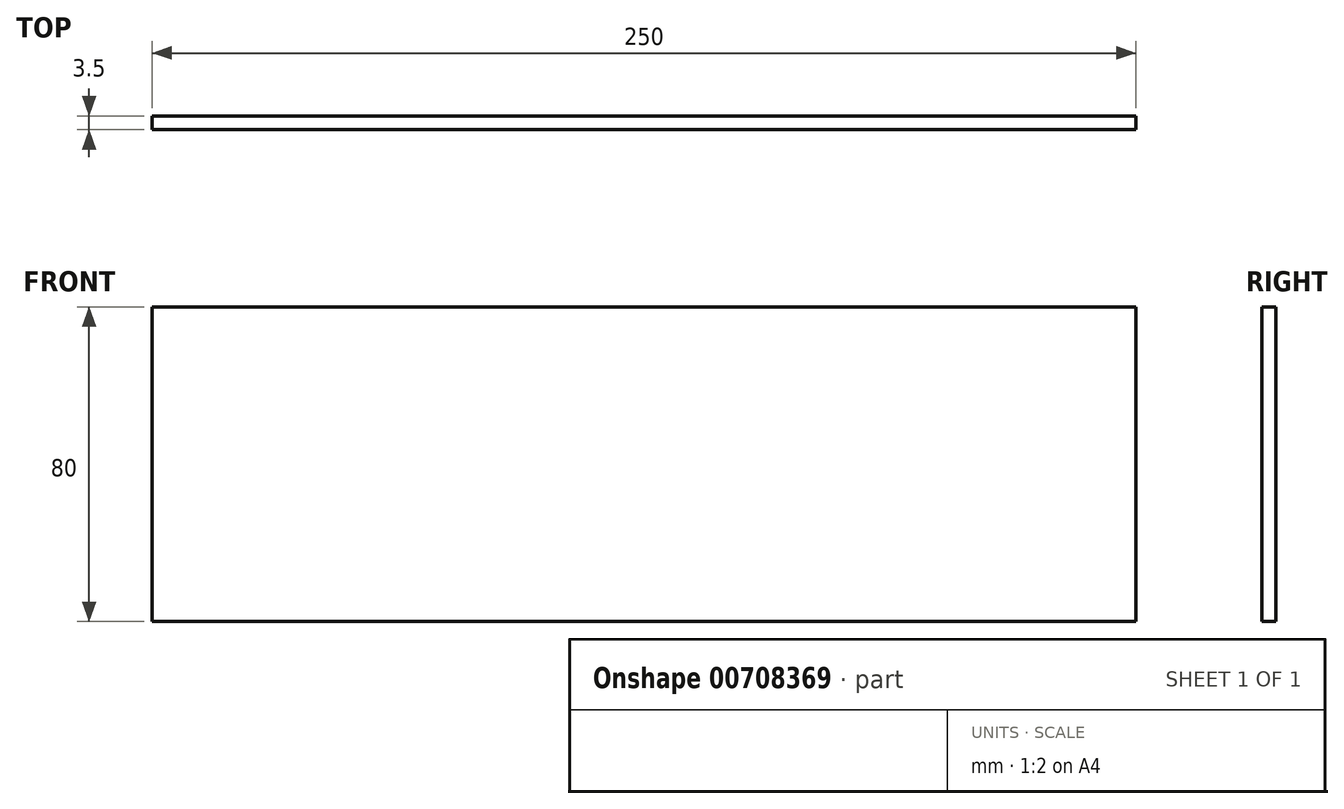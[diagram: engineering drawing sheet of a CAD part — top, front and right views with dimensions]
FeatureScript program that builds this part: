
annotation { "Feature Type Name" : "Feature", "Feature Type Description" : "" }
export const myFeature = defineFeature(function(context is Context, id is Id, definition is map)
    precondition{}
    {
        {
            var Q0;
            Q0=qCreatedBy(makeId("Right.planeOp"),FACE);
            var sketch = newSketch(context, id + "F0", { "sketchPlane" : qUnion([Q0])});
            skLineSegment(sketch, "E0", {"start": v(0, 0) * mm, "end": v(0, 80) * mm});
            skLineSegment(sketch, "E1", {"start": v(0, 80) * mm, "end": v(-3.5, 80) * mm});
            skLineSegment(sketch, "E2", {"start": v(-3.5, 80) * mm, "end": v(-3.5, 0) * mm});
            skLineSegment(sketch, "E3", {"start": v(-3.5, 0) * mm, "end": v(0, 0) * mm});
            skSolve(sketch);
        }
        {
            var Q0;
            Q0 = qSketchRegion(id + "F0", true);
            extrude(context, id + "F1", {"entities" : qUnion([Q0]), "endBound" : BoundingType.SYMMETRIC, "depth" : 250 * mm, "offsetDistance" : 25 * mm});
        }
    });
